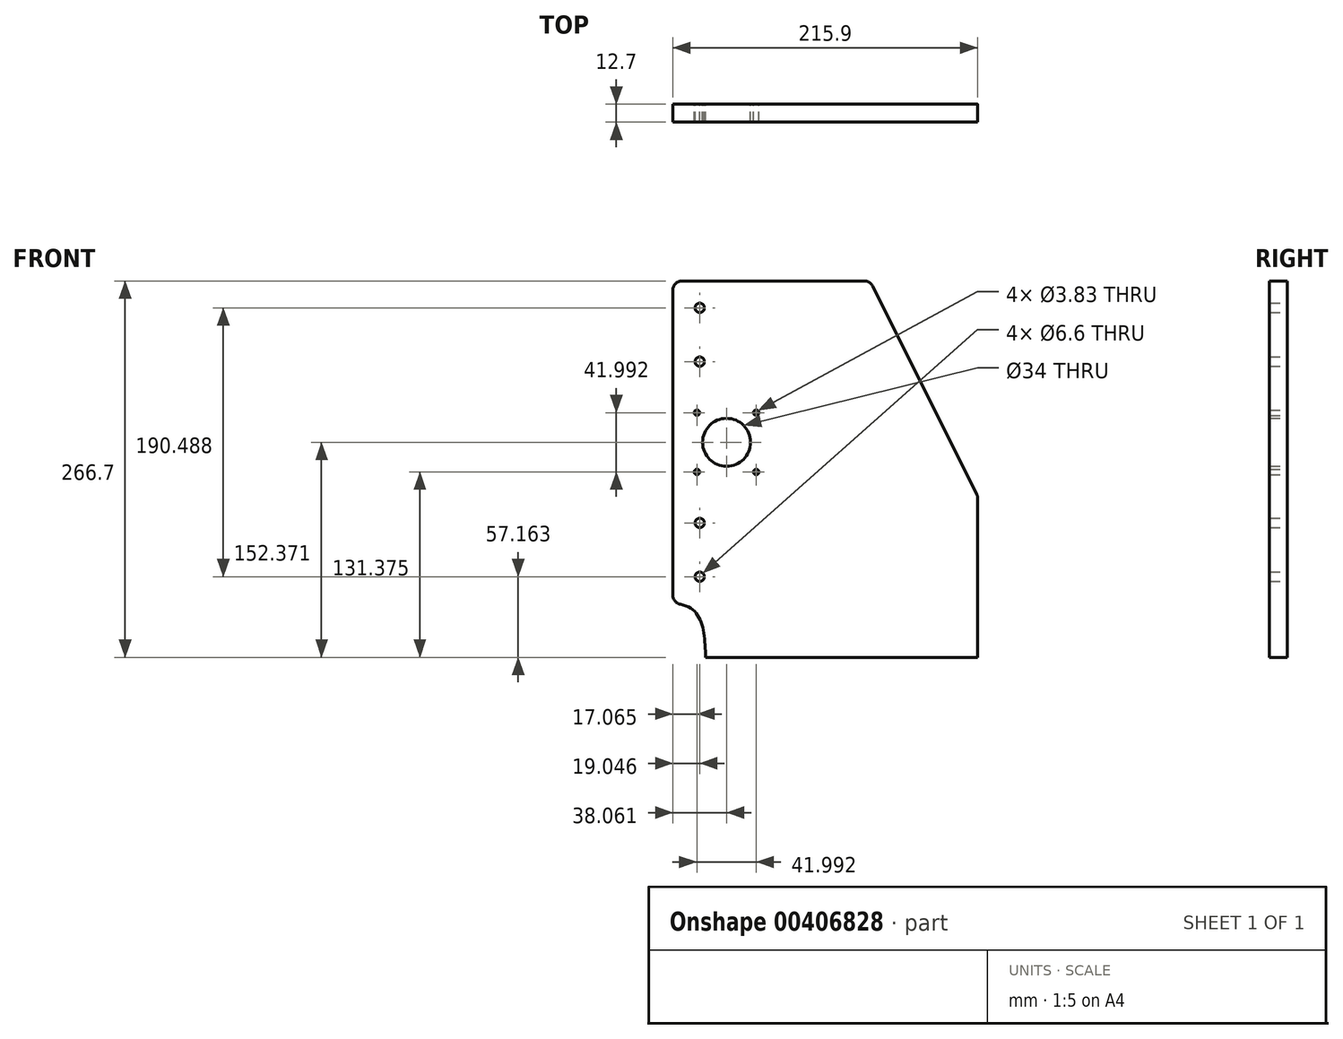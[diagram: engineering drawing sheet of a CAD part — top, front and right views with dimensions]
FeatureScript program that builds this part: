
annotation { "Feature Type Name" : "Feature", "Feature Type Description" : "" }
export const myFeature = defineFeature(function(context is Context, id is Id, definition is map)
    precondition{}
    {
        {
            var Q0;
            Q0=qCreatedBy(makeId("Front.planeOp"),FACE);
            var sketch = newSketch(context, id + "F0", { "sketchPlane" : qUnion([Q0])});
            skLineSegment(sketch, "E0.bottom", {"start": v(108.43, 152.4) * mm, "end": v(-107.47, 152.4) * mm});
            skLineSegment(sketch, "E0.left", {"start": v(108.43, 152.4) * mm, "end": v(108.43, -114.3) * mm});
            skLineSegment(sketch, "E0.right", {"start": v(-107.47, 152.4) * mm, "end": v(-107.47, -114.3) * mm});
            skPoint(sketch, "E0.middle", {"position": v(0, 0) * mm});
            skFitSpline(sketch, "E1", {"points": [v(-84.22, -114.3) * mm, v(-107.47, -76.2) * mm], "startDerivative": vector(-2.44, 55.55) * mm, "endDerivative": vector(-66.16, -0.04) * mm});
            skCircle(sketch, "E2", {"center": v(-88.42, -57.14) * mm, "radius": 3.3 * mm});
            skCircle(sketch, "E3", {"center": v(-88.42, -19.04) * mm, "radius": 3.3 * mm});
            skCircle(sketch, "E4", {"center": v(-88.42, 95.25) * mm, "radius": 3.3 * mm});
            skCircle(sketch, "E5", {"center": v(-88.42, 133.35) * mm, "radius": 3.3 * mm});
            skLineSegment(sketch, "E6", {"start": v(32.23, 152.4) * mm, "end": v(108.43, 0) * mm});
            skLineSegment(sketch, "E7", {"start": v(-107.47, -114.3) * mm, "end": v(108.43, -114.3) * mm});
            skLineSegment(sketch, "E8", {"start": v(-107.47, -76.2) * mm, "end": v(108.43, -76.2) * mm, "construction": true});
            skPoint(sketch, "E9.middle", {"position": v(-69.42, 38.11) * mm});
            skLineSegment(sketch, "E10", {"start": v(-69.42, 65.11) * mm, "end": v(-69.42, 11.11) * mm, "construction": true});
            skLineSegment(sketch, "E11", {"start": v(-96.42, 38.11) * mm, "end": v(-42.42, 38.11) * mm, "construction": true});
            skLineSegment(sketch, "E12.bottom", {"start": v(-43.4, 64.07) * mm, "end": v(-95.4, 64.07) * mm});
            skLineSegment(sketch, "E12.top", {"start": v(-43.4, 12.07) * mm, "end": v(-95.4, 12.07) * mm});
            skLineSegment(sketch, "E12.left", {"start": v(-43.4, 64.07) * mm, "end": v(-43.4, 12.07) * mm});
            skLineSegment(sketch, "E12.right", {"start": v(-95.4, 64.07) * mm, "end": v(-95.4, 12.07) * mm});
            skPoint(sketch, "E12.middle", {"position": v(-69.4, 38.07) * mm});
            skLineSegment(sketch, "E13", {"start": v(-95.4, 64.07) * mm, "end": v(-43.4, 12.07) * mm, "construction": true});
            skLineSegment(sketch, "E14", {"start": v(-43.4, 64.07) * mm, "end": v(-95.4, 12.07) * mm, "construction": true});
            skLineSegment(sketch, "E15", {"start": v(-69.4, 64.07) * mm, "end": v(-69.4, 12.07) * mm, "construction": true});
            skLineSegment(sketch, "E16", {"start": v(-43.4, 38.07) * mm, "end": v(-95.4, 38.07) * mm, "construction": true});
            skCircle(sketch, "E17", {"center": v(-90.4, 59.07) * mm, "radius": 1.91 * mm});
            skCircle(sketch, "E18.MirrorC", {"center": v(-90.4, 17.08) * mm, "radius": 1.91 * mm});
            skLineSegment(sketch, "E19.MirrorCS", {"start": v(-69.4, 12.07) * mm, "end": v(-69.4, 64.07) * mm, "construction": true});
            skCircle(sketch, "E20.MirrorC", {"center": v(-48.41, 59.07) * mm, "radius": 1.91 * mm});
            skCircle(sketch, "E21.MirrorC", {"center": v(-48.41, 17.08) * mm, "radius": 1.91 * mm});
            skCircle(sketch, "E22", {"center": v(-69.4, 38.07) * mm, "radius": 5 * mm});
            skCircle(sketch, "E23", {"center": v(-69.4, 38.07) * mm, "radius": 17 * mm});
            skPoint(sketch, "E24.startSnap0", {"position": v(0.48, 152.4) * mm});
            skSolve(sketch);
        }
        {
            var Q0;
            {var subQ3=sQuery(id+"F0.wireOp",EDGE,"E1");Q0=makeQuery(id+"F0.imprint","IMPRINT",FACE,{"disambiguationData":[TD([[makeQuery(id+"F0.imprint","IMPRINT",EDGE,{"derivedFrom":subQ3}),-1.0]])]});}
            var Q1;
            Q1=makeQuery(id+"F0.imprint","IMPRINT",FACE,{"disambiguationData":[TD([[makeQuery(id+"F0.imprint","IMPRINT",EDGE,{"derivedFrom":sQuery(id+"F0.wireOp",EDGE,"E12.bottom")}),1.0]])]});
            extrude(context, id + "F1", {"entities" : qUnion([Q0, Q1]), "depth" : 12.7 * mm});
        }
        {
            var Q0;
            {var subQ2=sQuery(id+"F0.wireOp",EDGE,"E1");Q0=makeQuery(id+"F0.imprint","IMPRINT",FACE,{"disambiguationData":[TD([[makeQuery(id+"F0.imprint","IMPRINT",EDGE,{"derivedFrom":subQ2}),-1.0]])]});}
            extrude(context, id + "F2", {"entities" : qUnion([Q0]), "operationType" : NewBodyOperationType.REMOVE, "oppositeDirection" : true, "depth" : 25.4 * mm});
        }
        {
            var Q0;
            Q0=makeQuery(id+"F1.opExtrude","SWEPT_EDGE",EDGE,{"disambiguationData":[OSD([sQuery(id+"F0.wireOp",EDGE,"E0.bottom"),sQuery(id+"F0.wireOp",EDGE,"E0.right")])]});
            var Q1;
            Q1=makeQuery(id+"F1.opExtrude","SWEPT_EDGE",EDGE,{"disambiguationData":[OSD([sQuery(id+"F0.wireOp",EDGE,"E0.bottom"),sQuery(id+"F0.wireOp",EDGE,"E24")])]});
            var Q2;
            Q2=makeQuery(id+"F1.opExtrude","SWEPT_EDGE",EDGE,{"disambiguationData":[OSD([sQuery(id+"F0.wireOp",EDGE,"E0.right"),sQuery(id+"F0.wireOp",EDGE,"E1")])]});
            var Q3;
            Q3=makeQuery(id+"F1.opExtrude","SWEPT_EDGE",EDGE,{"disambiguationData":[OSD([sQuery(id+"F0.wireOp",EDGE,"E0.left"),sQuery(id+"F0.wireOp",EDGE,"E6")])]});
            fillet(context, id + "F3", {"entities" : qUnion([Q0, Q1, Q2, Q3]), "radius" : 6.35 * mm, "tangentPropagation" : true, "allowEdgeOverflow" : false});
        }
    });
